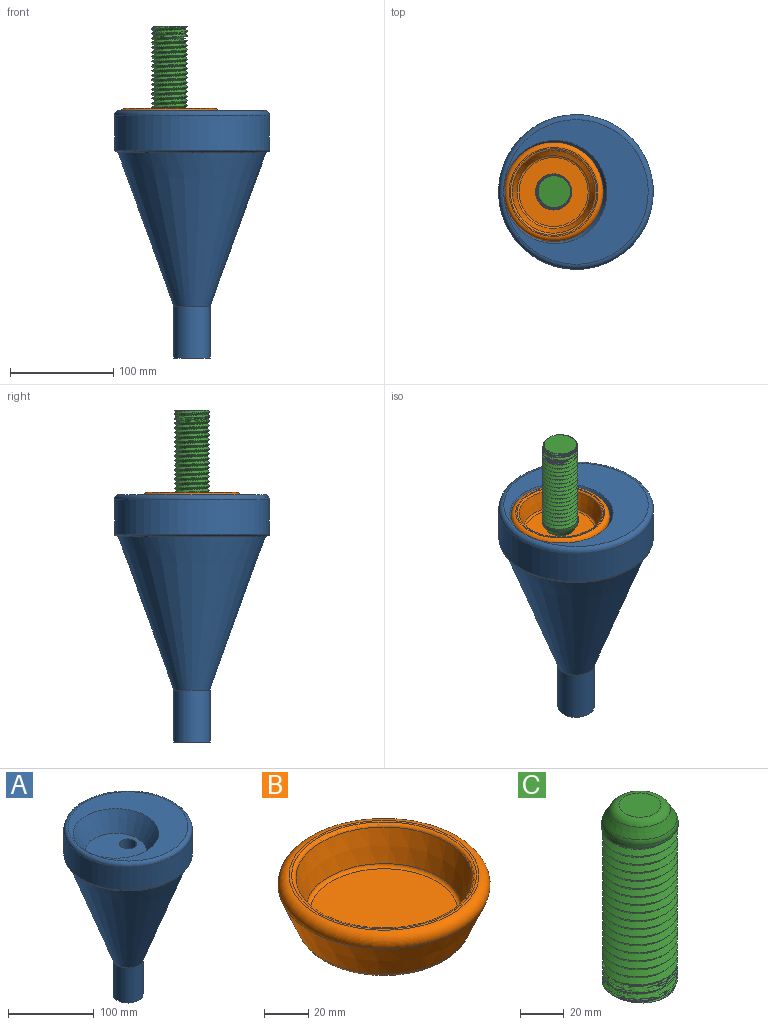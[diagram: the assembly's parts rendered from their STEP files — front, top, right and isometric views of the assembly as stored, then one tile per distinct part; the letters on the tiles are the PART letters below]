
ASSEMBLY  parts=3 mates=2
PART A: 13 faces, bbox 162.4x162.4x240 mm
  f0: plane 140x140mm, normal (0,0,1), area 7539.8mm2, adj f1,f12
  f1: cone r=50mm half-angle=30deg, axis (0,0,1), area 7760mm2, adj f0,f2
  f2: plane 71.13x71.13mm, normal (0,0,1), area 3659.8mm2, adj f1,f9
  f3: cylinder r=75mm len=150mm, axis (0,0,1), area 15786.5mm2, adj f11,f12
  f4: plane 147x147mm, normal (0,0,-1), area 207mm2, adj f10,f11
  f5: cone r=72mm half-angle=20deg, axis (0,0,1), area 44360.8mm2, adj f8,f10
  f6: cylinder r=17.5mm len=50mm, axis (0,0,1), area 5497.8mm2, adj f7,f8
  f7: plane 35x35mm, normal (0,0,-1), area 648mm2, adj f6,f9
  f8: plane 35x35mm, normal (0,0,1), area 10.5mm2, adj f5,f6
  f9: cylinder r=10mm len=215mm, axis (0,0,-1), area 13508.8mm2, adj f2,f7
  f10: torus R=73.05mm, axis (0,0,1), area 831.8mm2, adj f4,f5
  f11: torus R=73.5mm, axis (0,0,1), area 1102.3mm2, adj f3,f4
  f12: torus R=70mm, axis (0,0,1), area 3611.4mm2, adj f0,f3
PART B: 9 faces, bbox 104x104x30 mm
  f0: cone r=40mm half-angle=23deg, axis (0,0,1), area 5926.9mm2, adj f3,f4
  f1: plane 86.12x86.12mm, normal (0,0,1), area 310.7mm2, adj f3,f7
  f2: plane 69.14x69.14mm, normal (0,0,-1), area 3754.1mm2, adj f4
  f3: torus R=43.06mm, axis (0,0,1), area 2886.3mm2, adj f0,f1
  f4: torus R=34.57mm, axis (0,0,1), area 1365.6mm2, adj f0,f2
  f5: cone r=35mm half-angle=15deg, axis (0,0,1), area 4175.3mm2, adj f7,f8
  f6: plane 66.93x66.93mm, normal (0,0,1), area 3518.4mm2, adj f8
  f7: torus R=41.89mm, axis (0,0,1), area 670.5mm2, adj f1,f5
  f8: torus R=33.47mm, axis (0,0,1), area 569.1mm2, adj f5,f6
PART C: 10 faces, bbox 37.9x40.4x102.5 mm
  f0: cylinder r=17.5mm len=35mm, axis (0,0,-1), area 247.4mm2, adj f3,f7,f8
  f1: plane 19.23x19.23mm, normal (0,0,1), area 290.3mm2, adj f4
  f2: cone r=12.5mm half-angle=30deg, axis (0,0,-1), area 558.2mm2, adj f3,f4
  f3: torus R=12.5mm, axis (0,0,1), area 284.2mm2, adj f0,f2
  f4: torus R=9.61mm, axis (0,0,1), area 394.8mm2, adj f1,f2
  f5: bspline ~90x39.84mm, area 6202.1mm2, adj f6,f7,f9
  f6: bspline ~92.25x39.84mm, area 6356.9mm2, adj f5,f7,f8,f9
  f7: plane 4.75x2.5mm, normal (0,-1,0), area 6.2mm2, adj f0,f5,f6,f8
  f8: bspline ~40.41x35mm, area 38.6mm2, adj f0,f6,f7
  f9: plane 32.29x32.28mm, normal (0,0,-1), area 818.2mm2, adj f5,f6
PLACE A t=(25.8,22.04,0.06)mm
PLACE B t=(4.09,22.04,17.02)mm fixed
PLACE C rot(axis=(0.81,0.58,0),180deg) t=(4.09,22.04,122.02)mm
MATE fastened A.f2 <-> B.f0  axis (0,0,1) through (4.09,22.04,15.06)mm
MATE revolute C.f0 <-> B.f0  axis (0,0,-1) through (4.09,22.04,22.02)mm
